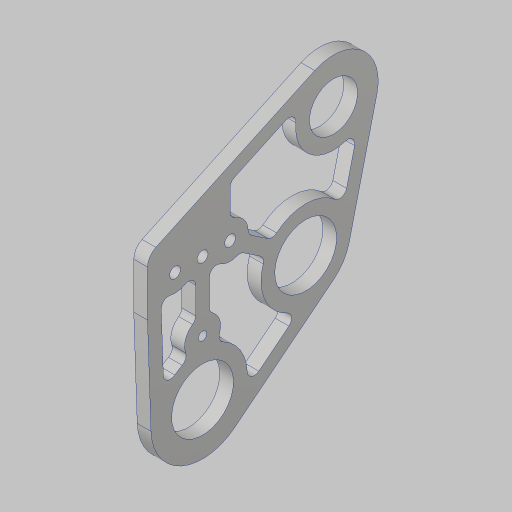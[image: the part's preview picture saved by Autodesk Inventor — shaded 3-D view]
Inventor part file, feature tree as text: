
AUTODESK INVENTOR PART (.ipt)
format: ipt  version: 2023.5 (Build 275446000, 446)  size: 310,272 bytes
history: native  units: in
note: dims shown in document units (in); Inventor stores cm internally (conversion verified against a paired STEP export)
features: sketch x3, extrude x2, hole x2, fillet x2, projected_geometry x2
ambient origin geometry x8: Origin, YZ Plane, XZ Plane, XY Plane, X Axis, Y Axis, Z Axis, Center Point
bodies: Solid1 (feature_tree)
feature tree (11):
  sketch  "Sketch1"  dims[d0=1.0in d1=2.0in]
  extrude  "Extrusion1"  Depth=2.0in
  hole  "Hole1"  [1 undecoded]
  hole  "Hole3"  [1 undecoded]
  extrude  "Extrusion2"  Depth=0.26in
  fillet  "Fillet1"  Radius=0.5in
  fillet  "Fillet2"  Radius=0.5in
  sketch  "Sketch2"  dims[d2=1.125in d3=2.25in]
  sketch  "Sketch3"  dims[d4=3.0in d5=5.0in d6=1.949in d11=0.5in d12=0.5in d13=0.375in d18=0.4688in d19=2.5in d20=1.375in d21=1.74in d22=8.0in d23=1.0in d24=2.1066in d25=0.25in d26=0.0in d29=2.3622in d31=360.0deg d33=0.201in d34=0.75in d35=0.385in d36=0.25in d37=0.5635in d38=1.0in d39=0.8108in d40=1.0in d41=3.3in d42=1.6in d43=3.0in d44=1.4348in d46=0.25in d48=0.5in d49=1.0in d50=0.875in d51=1.25in d52=0.75in d54=0.125in d62=0.875in d63=1.0in d64=0.156in d65=0.38in d66=0.385in d67=0.25in d68=0.5635in d69=1.0in d70=0.8108in d71=0.25in d72=0.25in d73=0.25in d74=0.25in d75=0.125in d76=0.125in d77=0.125in d78=0.125in d79=0.0in d80=0.0in d81=0.13in d82=0.26in]
  projected_geometry  "Project Cut Edges1"
  projected_geometry  "Project Cut Edges2"
note: 2 required parameter values undecoded (feature->parameter linkage not recoverable at this tier; creation-order binding heuristic only, values carry confidence <= 0.55)
